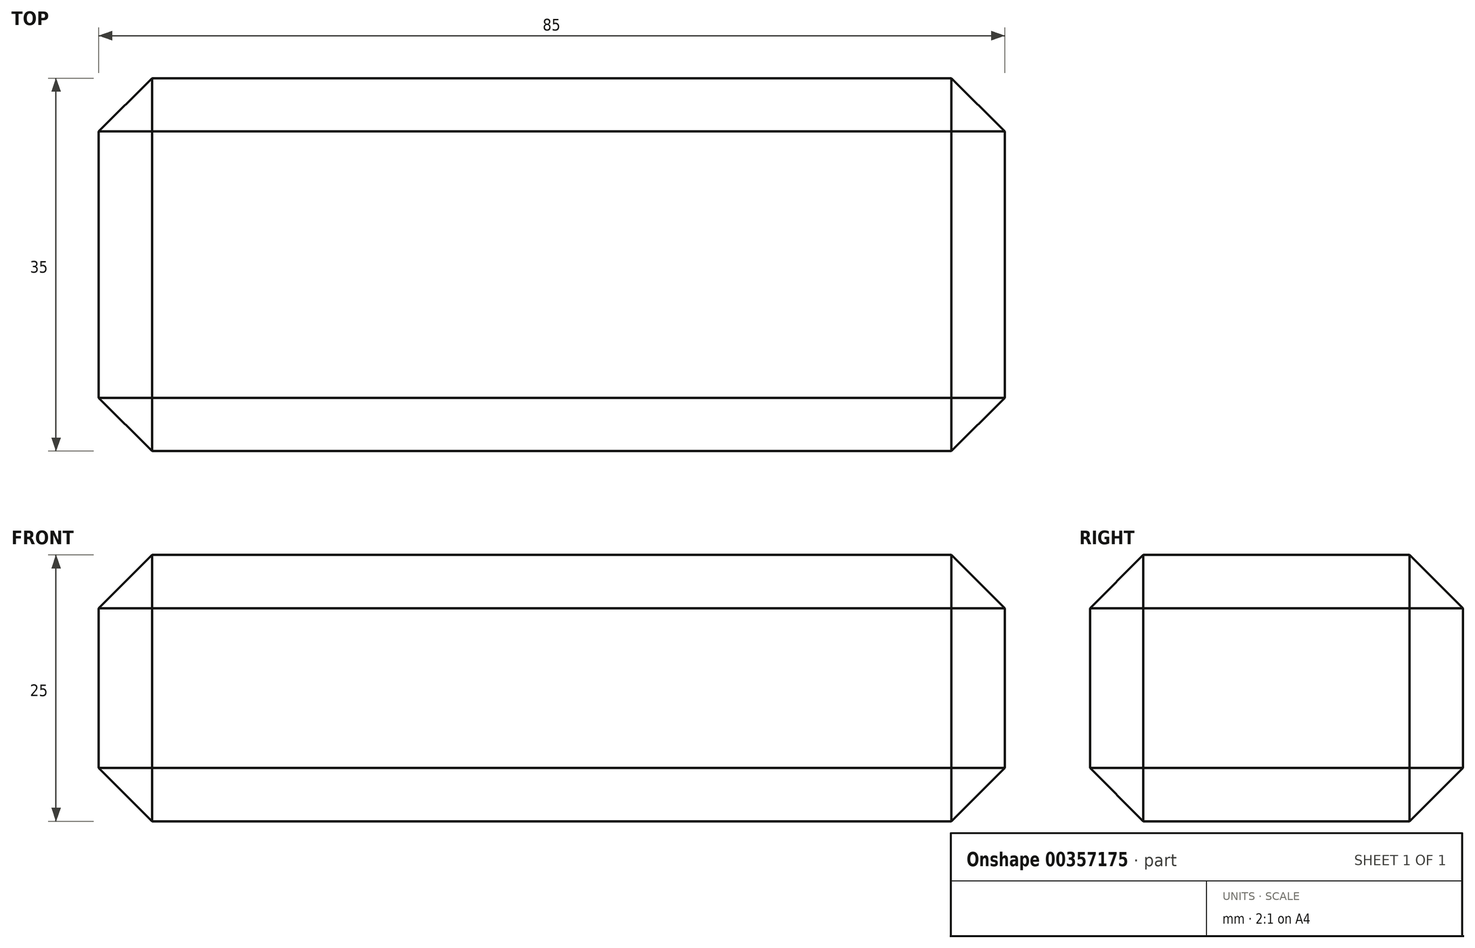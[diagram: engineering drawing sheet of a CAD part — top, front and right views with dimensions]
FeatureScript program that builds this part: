
annotation { "Feature Type Name" : "Feature", "Feature Type Description" : "" }
export const myFeature = defineFeature(function(context is Context, id is Id, definition is map)
    precondition{}
    {
        {
            var Q0;
            Q0=qCreatedBy(makeId("Top.planeOp"),FACE);
            var sketch = newSketch(context, id + "F0", { "sketchPlane" : qUnion([Q0])});
            skLineSegment(sketch, "E0.bottom", {"start": v(-42.5, 17.5) * mm, "end": v(42.5, 17.5) * mm});
            skLineSegment(sketch, "E0.top", {"start": v(-42.5, -17.5) * mm, "end": v(42.5, -17.5) * mm});
            skLineSegment(sketch, "E0.left", {"start": v(-42.5, 17.5) * mm, "end": v(-42.5, -17.5) * mm});
            skLineSegment(sketch, "E0.right", {"start": v(42.5, 17.5) * mm, "end": v(42.5, -17.5) * mm});
            skPoint(sketch, "E0.middle", {"position": v(0, 0) * mm});
            skSolve(sketch);
        }
        {
            var Q0;
            Q0 = qSketchRegion(id + "F0", true);
            extrude(context, id + "F1", {"entities" : qUnion([Q0]), "depth" : 25 * mm});
        }
        {
            var Q0;
            Q0=makeQuery(id+"F1.opExtrude","CAP_EDGE",EDGE,{"disambiguationData":[OSD([sQuery(id+"F0.wireOp",EDGE,"E0.bottom")])],"isStart":false});
            var Q1;
            Q1=makeQuery(id+"F1.opExtrude","CAP_EDGE",EDGE,{"disambiguationData":[OSD([sQuery(id+"F0.wireOp",EDGE,"E0.bottom")])],"isStart":true});
            var Q2;
            Q2=makeQuery(id+"F1.opExtrude","SWEPT_EDGE",EDGE,{"disambiguationData":[OSD([sQuery(id+"F0.wireOp",EDGE,"E0.bottom"),sQuery(id+"F0.wireOp",EDGE,"E0.right")])]});
            var Q3;
            Q3=makeQuery(id+"F1.opExtrude","SWEPT_EDGE",EDGE,{"disambiguationData":[OSD([sQuery(id+"F0.wireOp",EDGE,"E0.bottom"),sQuery(id+"F0.wireOp",EDGE,"E0.left")])]});
            var Q4;
            Q4=makeQuery(id+"F1.opExtrude","CAP_EDGE",EDGE,{"disambiguationData":[OSD([sQuery(id+"F0.wireOp",EDGE,"E0.left")])],"isStart":false});
            var Q5;
            Q5=makeQuery(id+"F1.opExtrude","CAP_EDGE",EDGE,{"disambiguationData":[OSD([sQuery(id+"F0.wireOp",EDGE,"E0.left")])],"isStart":true});
            var Q6;
            Q6=makeQuery(id+"F1.opExtrude","CAP_EDGE",EDGE,{"disambiguationData":[OSD([sQuery(id+"F0.wireOp",EDGE,"E0.top")])],"isStart":true});
            var Q7;
            Q7=makeQuery(id+"F1.opExtrude","CAP_EDGE",EDGE,{"disambiguationData":[OSD([sQuery(id+"F0.wireOp",EDGE,"E0.right")])],"isStart":false});
            var Q8;
            Q8=makeQuery(id+"F1.opExtrude","CAP_EDGE",EDGE,{"disambiguationData":[OSD([sQuery(id+"F0.wireOp",EDGE,"E0.right")])],"isStart":true});
            var Q9;
            Q9=makeQuery(id+"F1.opExtrude","CAP_EDGE",EDGE,{"disambiguationData":[OSD([sQuery(id+"F0.wireOp",EDGE,"E0.top")])],"isStart":false});
            var Q10;
            Q10=makeQuery(id+"F1.opExtrude","SWEPT_EDGE",EDGE,{"disambiguationData":[OSD([sQuery(id+"F0.wireOp",EDGE,"E0.top"),sQuery(id+"F0.wireOp",EDGE,"E0.right")])]});
            var Q11;
            Q11=makeQuery(id+"F1.opExtrude","SWEPT_EDGE",EDGE,{"disambiguationData":[OSD([sQuery(id+"F0.wireOp",EDGE,"E0.top"),sQuery(id+"F0.wireOp",EDGE,"E0.left")])]});
            chamfer(context, id + "F2", {"entities" : qUnion([Q0, Q1, Q2, Q3, Q4, Q5, Q6, Q7, Q8, Q9, Q10, Q11]), "width" : 5 * mm, "tangentPropagation" : true});
        }
    });
